# Revit family: Haworth_Masters_StorageTower
name_source: partatom
category: Furniture Systems
revit_build: Autodesk Revit 2018 (Build: 20170223_1515(x64)
units: mm (PartAtom-declared; Revit-internal decimal feet)

## family parameters
Always vertical = Yes
Cut with Voids When Loaded = No
OmniClass Number = 23.40.70.14.64.21
OmniClass Title = Systems Furniture
Part Type = Normal
Room Calculation Point = No
Round Connector Dimension = Use Diameter
Shared = No
Work Plane-Based = No

## types (4) — shared parameters
Actual Width = 15 1/2"
Assembly Code = E2020200
Bar Pull = Yes
Base Height = 2 35/64"
Classic Pull = No
Door Offset = 28"
Door Pull Offset = 1 1/2"
Door Width = 15 1/2"
Drawer 1 Offset = 2 11/16"
Drawer 2 Offset = 15 3/8"
Drawer Height = 12 35/64"
Drawer Inside Height = 27 59/64"
Finger Pull = No
Fixed Shelf Height = 27 59/64"
Linear Pull = No
Lock Offset Centerline = 3"
Manufacturer = Haworth
Max. Depth = 24"
Max. Height = 81 5/8"
Min. Depth = 19"
Min. Height = 69"
Model = Haworth Masters
Panel Thickness = 23/32"
Pull Offset Centerline = 3"
Revision Number = 1
Shelf Offset = 40 69/128"
Shelf Width = 14 1/16"
Size = Verify Final Dim. w/ Haworth
URL = www.haworth.com
URL - Product = http://www.haworth.com
Warranty = http://www.haworth.com

## per-type parameters (varying)
| type | # of Shelves | 19in. Depth | 24in. Depth | 69in. Height | 81in. Height | Actual Depth | Actual Height | Description | Door Height | Shelf Depth | Shelf Spacing | Sustainability Info |
| 15w 19d 82h | 3 | Yes | No | No | Yes | 19" | 81 5/8" | Haworth - Masters - Storage Tower - 15w 19d 82h | 53 9/16" | 17 9/16" | 13 89/128" | http://www.haworth.com |
| 15w 19d 69h | 2 | Yes | No | Yes | No | 19" | 69" | Haworth - Masters - Storage Tower - 15w 19d 69h | 40 15/16" | 17 9/16" | 14 59/256" | http://www.haworth.com |
| 15w 24d 82h | 3 | No | Yes | No | Yes | 24" | 81 5/8" | Haworth - Masters - Storage Tower - 15w 24d 82h | 53 9/16" | 22 9/16" | 13 89/128" | https://www.haworth.com |
| 15w 24d 69h | 2 | No | Yes | Yes | No | 24" | 69" | Haworth - Masters - Storage Tower - 15w 24d 69h | 40 15/16" | 22 9/16" | 14 59/256" | http://www.haworth.com |

## geometry (parser evidence)
native form markers: Sweep x13
no freeform markers — native parametric forms only
